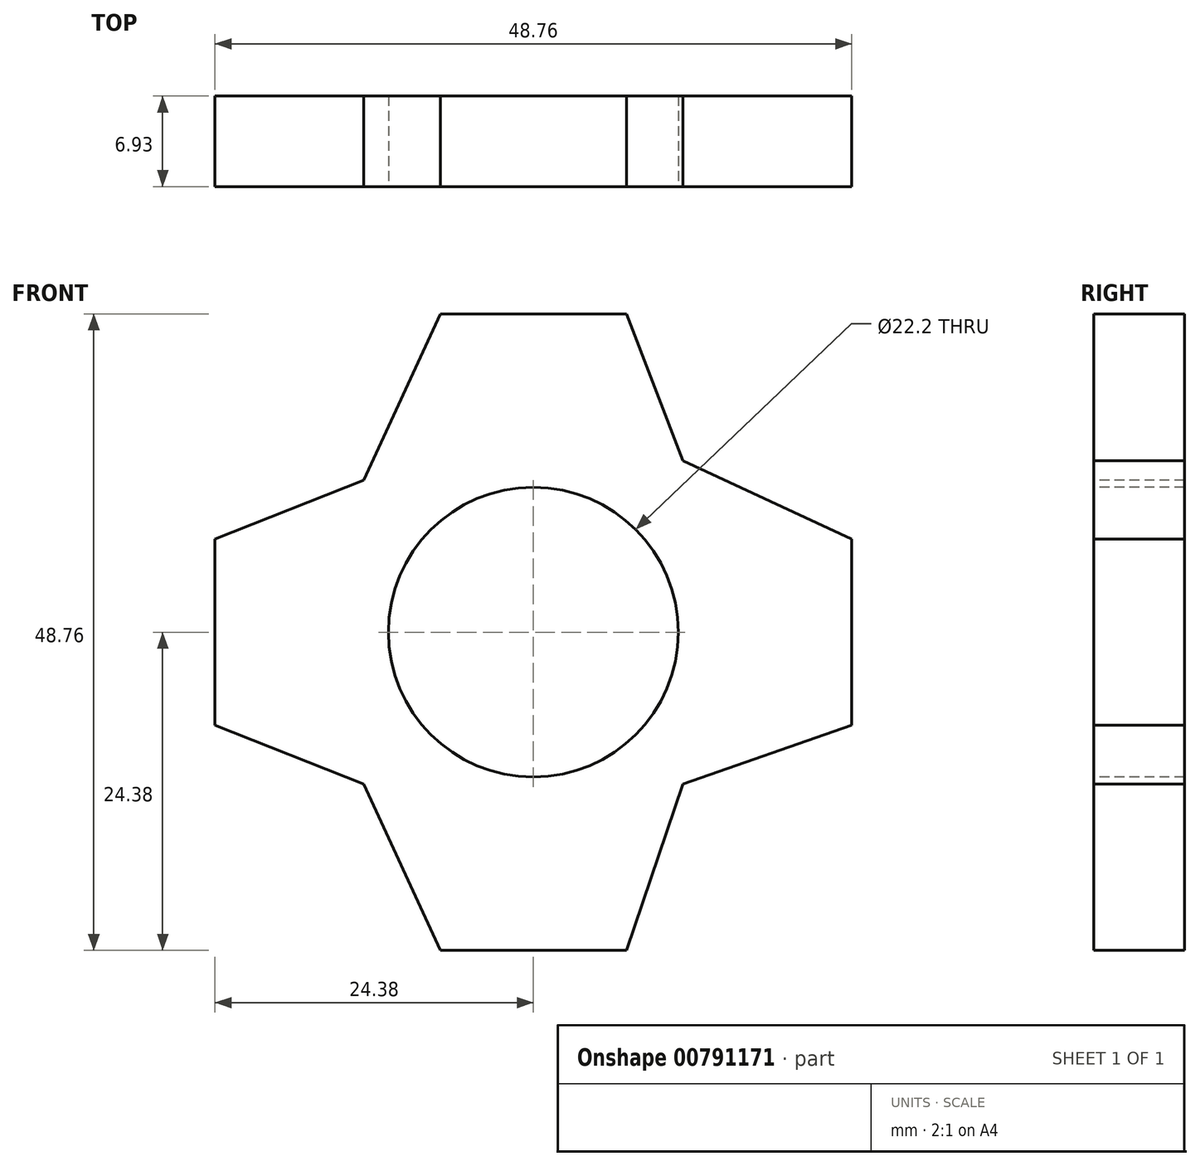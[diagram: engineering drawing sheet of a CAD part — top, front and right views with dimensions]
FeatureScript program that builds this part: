
annotation { "Feature Type Name" : "Feature", "Feature Type Description" : "" }
export const myFeature = defineFeature(function(context is Context, id is Id, definition is map)
    precondition{}
    {
        {
            var Q0;
            Q0=qCreatedBy(makeId("Front.planeOp"),FACE);
            var sketch = newSketch(context, id + "F0", { "sketchPlane" : qUnion([Q0])});
            skCircle(sketch, "E0", {"center": v(0, 0) * mm, "radius": 11.1 * mm});
            skLineSegment(sketch, "E1", {"start": v(-7.13, 24.38) * mm, "end": v(7.13, 24.38) * mm});
            skLineSegment(sketch, "E2", {"start": v(7.13, 24.38) * mm, "end": v(11.47, 13.13) * mm});
            skLineSegment(sketch, "E3", {"start": v(24.38, 7.13) * mm, "end": v(24.38, -7.13) * mm});
            skLineSegment(sketch, "E4", {"start": v(-24.38, -7.13) * mm, "end": v(-24.38, 7.13) * mm});
            skLineSegment(sketch, "E5", {"start": v(7.13, -24.38) * mm, "end": v(-7.13, -24.38) * mm});
            skLineSegment(sketch, "E6", {"start": v(11.47, 13.13) * mm, "end": v(24.38, 7.13) * mm});
            skLineSegment(sketch, "E7", {"start": v(24.38, -7.13) * mm, "end": v(11.47, -11.64) * mm});
            skLineSegment(sketch, "E8", {"start": v(11.47, -11.64) * mm, "end": v(7.13, -24.38) * mm});
            skLineSegment(sketch, "E9", {"start": v(-7.13, -24.38) * mm, "end": v(-12.98, -11.64) * mm});
            skLineSegment(sketch, "E10", {"start": v(-12.98, -11.64) * mm, "end": v(-24.38, -7.13) * mm});
            skLineSegment(sketch, "E11", {"start": v(-24.38, 7.13) * mm, "end": v(-12.98, 11.64) * mm});
            skLineSegment(sketch, "E12", {"start": v(-7.13, 24.38) * mm, "end": v(-12.98, 11.64) * mm});
            skCircle(sketch, "E13", {"center": v(0, 0) * mm, "radius": 25.4 * mm, "construction": true});
            skCircle(sketch, "E14", {"center": v(0, 0) * mm, "radius": 17.43 * mm, "construction": true});
            skSolve(sketch);
        }
        {
            var Q0;
            Q0=makeQuery(id+"F0.imprint","IMPRINT",FACE,{"disambiguationData":[TD([[makeQuery(id+"F0.imprint","IMPRINT",EDGE,{"derivedFrom":sQuery(id+"F0.wireOp",EDGE,"E0")}),-1.0]])]});
            extrude(context, id + "F1", {"entities" : qUnion([Q0]), "oppositeDirection" : true, "depth" : 6.93 * mm, "offsetDistance" : 25.4 * mm});
        }
    });
